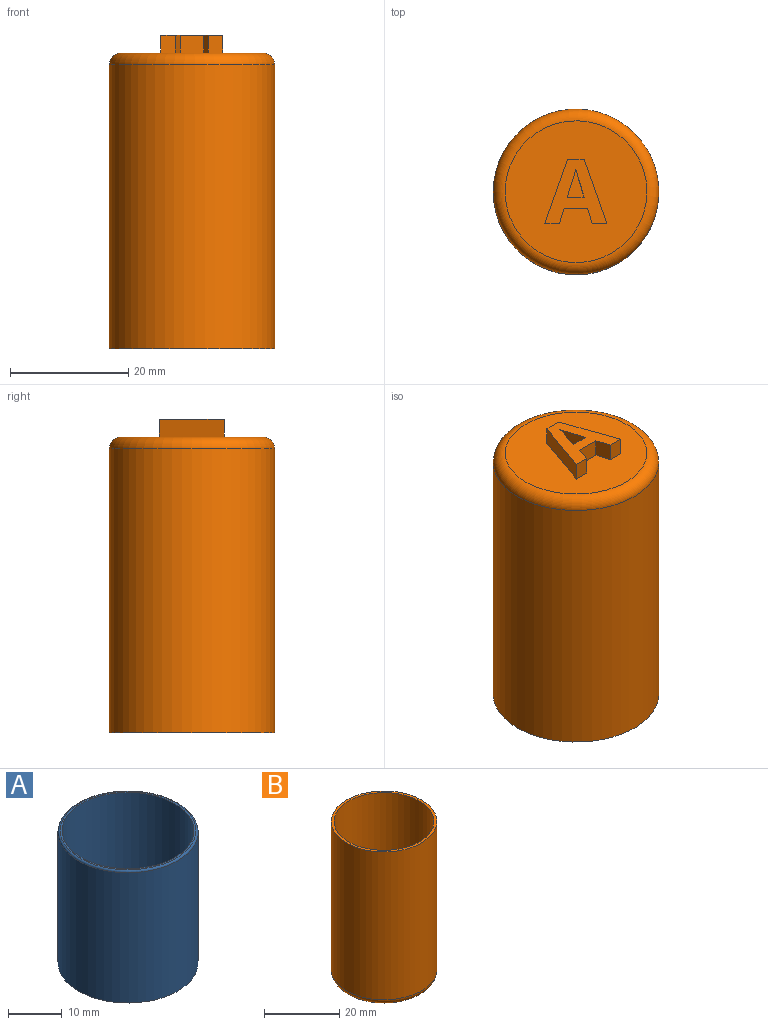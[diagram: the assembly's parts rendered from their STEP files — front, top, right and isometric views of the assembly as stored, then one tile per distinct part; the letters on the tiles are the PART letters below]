
ASSEMBLY  parts=2 mates=1
PART A: 6 faces, bbox 28.1x28.1x30 mm
  f0: cylinder r=13mm len=29.6mm, axis (0,0,-1), area 2417.8mm2, adj f2,f5
  f1: plane 25.2x25.2mm, normal (0,0,1), area 27.3mm2, adj f3,f5
  f2: plane 26x26mm, normal (0,0,-1), area 530.9mm2, adj f0
  f3: cylinder r=12.25mm len=28mm, axis (0,0,1), area 2155.1mm2, adj f1,f4
  f4: plane 24.5x24.5mm, normal (0,0,1), area 471.4mm2, adj f3
  f5: torus R=12.6mm, axis (0,0,1), area 50.7mm2, adj f0,f1
PART B: 20 faces, bbox 30.3x30.3x53 mm
  f0: plane 24x24mm, normal (0,0,-1), area 391.6mm2, adj f5,f9,f10,f11,f12,f13,f14,f15
  f1: cylinder r=14mm len=48mm, axis (0,0,-1), area 4222.3mm2, adj f2,f5
  f2: plane 28x28mm, normal (0,0,1), area 64.2mm2, adj f1,f3
  f3: cylinder r=13.25mm len=27.5mm, axis (0,0,1), area 2289.4mm2, adj f2,f4
  f4: plane 26.5x26.5mm, normal (0,0,1), area 551.5mm2, adj f3
  f5: torus R=12mm, axis (0,0,1), area 262mm2, adj f0,f1
  f6: extruded ~3.99x3mm, area 12.5mm2, adj f7,f17,f18,f19
  f7: plane 3x2.84mm, normal (0,1,0), area 8.5mm2, adj f6,f8,f18,f19
  f8: extruded ~4.72x3mm, area 14.8mm2, adj f7,f17,f18,f19
  f9: plane 3x2.6mm, normal (-0.96,-0.29,0), area 8.1mm2, adj f0,f10,f16,f18
  f10: plane 3x2.49mm, normal (0,-1,0), area 7.5mm2, adj f0,f9,f11,f18
  f11: plane 10.95x3.86mm, normal (0.94,0.33,0), area 34.8mm2, adj f0,f10,f12,f18
  f12: plane 3x2.83mm, normal (0,1,0), area 8.5mm2, adj f0,f11,f13,f18
  f13: plane 10.95x3.85mm, normal (-0.94,0.33,0), area 34.8mm2, adj f0,f12,f14,f18
  f14: plane 3x2.49mm, normal (0,-1,0), area 7.5mm2, adj f0,f13,f15,f18
  f15: plane 3x2.6mm, normal (0.96,-0.29,0), area 8.1mm2, adj f0,f14,f16,f18
  f16: plane 3.98x3mm, normal (0,-1,0), area 11.9mm2, adj f0,f9,f15,f18
  f17: extruded ~3x0.73mm, area 2.3mm2, adj f6,f8,f18,f19
  f18: plane 10.95x10.54mm, normal (0,0,-1), area 54.2mm2, adj f6,f7,f8,f9,f10,f11,f12,f13
  f19: plane 4.72x2.84mm, normal (0,0,-1), area 6.6mm2, adj f6,f7,f8,f17
PLACE A t=(-3.86,6.14,-4.65)mm fixed
PLACE B rot(axis=(0,1,0),180deg) t=(-3.86,6.14,43.74)mm
MATE cylindrical A.f0 <-> B.f3  axis (0,0,1) through (-3.86,6.14,25.35)mm
